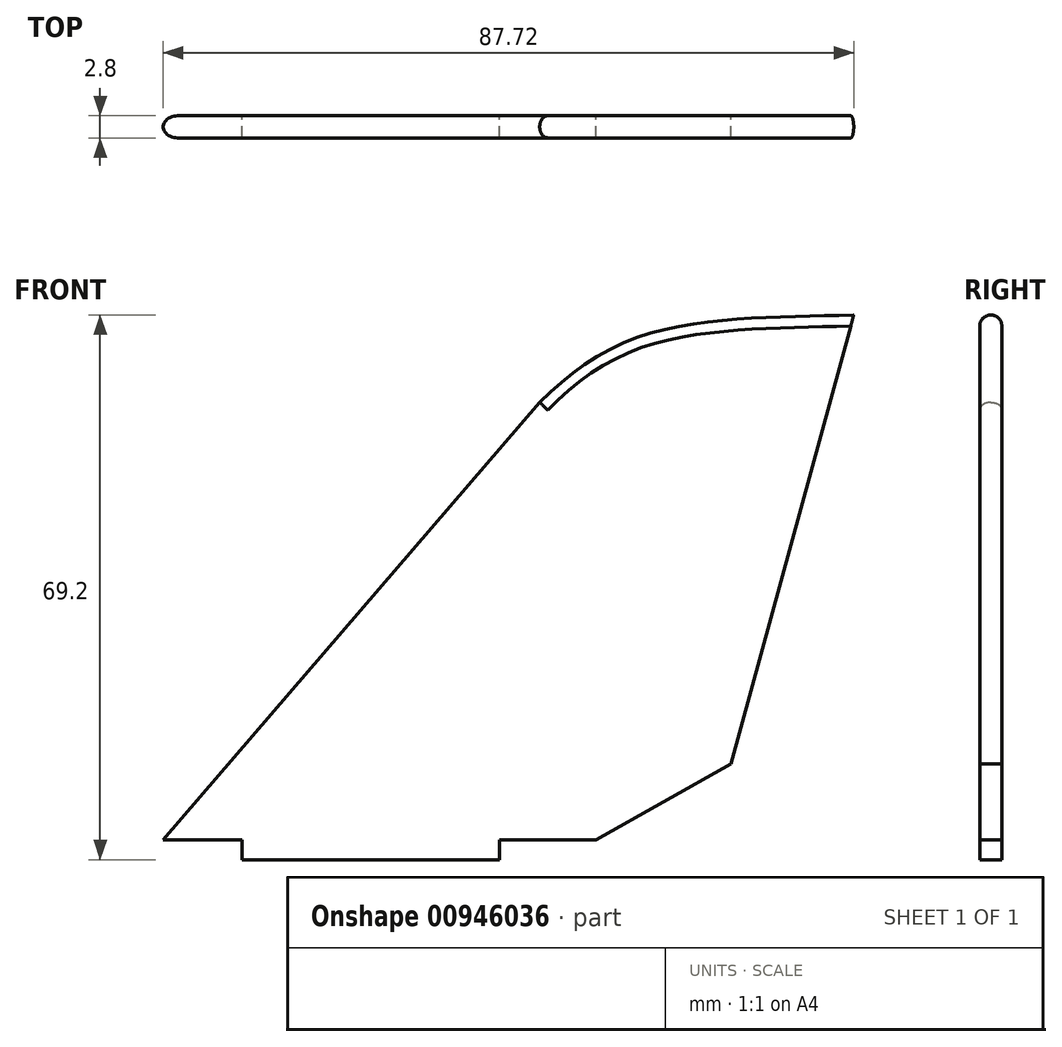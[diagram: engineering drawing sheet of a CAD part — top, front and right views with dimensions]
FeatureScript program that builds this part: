
annotation { "Feature Type Name" : "Feature", "Feature Type Description" : "" }
export const myFeature = defineFeature(function(context is Context, id is Id, definition is map)
    precondition{}
    {
        {
            var Q0;
            Q0=qCreatedBy(makeId("Front.planeOp"),FACE);
            var sketch = newSketch(context, id + "F0", { "sketchPlane" : qUnion([Q0])});
            skLineSegment(sketch, "E0.bottom", {"start": v(20, -28.75) * mm, "end": v(-35, -28.75) * mm});
            skLineSegment(sketch, "E0.right", {"start": v(-35, -28.75) * mm, "end": v(-35, -26.25) * mm});
            skPoint(sketch, "E0.middle", {"position": v(0, 0) * mm});
            skLineSegment(sketch, "E1", {"start": v(-35, -26.25) * mm, "end": v(-25, -26.25) * mm});
            skLineSegment(sketch, "E2", {"start": v(-35, -26.25) * mm, "end": v(3.21, 18.18) * mm});
            skPoint(sketch, "E3", {"position": v(20, -26.25) * mm});
            skPoint(sketch, "E4.orphan", {"position": v(-35, 28.75) * mm});
            skLineSegment(sketch, "E5", {"start": v(20, -26.25) * mm, "end": v(20, -28.75) * mm});
            skPoint(sketch, "E0.left.end.orphan", {"position": v(35, -8.81) * mm});
            skPoint(sketch, "E6.orphan", {"position": v(35, -28.75) * mm});
            skLineSegment(sketch, "E7", {"start": v(-25, -26.25) * mm, "end": v(-25, -28.75) * mm});
            skLineSegment(sketch, "E8", {"start": v(7.7, -26.25) * mm, "end": v(7.7, -28.75) * mm});
            skLineSegment(sketch, "E9.trimOffspring", {"start": v(7.7, -26.25) * mm, "end": v(20, -26.25) * mm});
            skLineSegment(sketch, "E10", {"start": v(20, -26.25) * mm, "end": v(37.1, -16.57) * mm});
            skLineSegment(sketch, "E11", {"start": v(37.1, -16.57) * mm, "end": v(52.72, 40.45) * mm});
            skLineSegment(sketch, "E12", {"start": v(-5.1, 8.52) * mm, "end": v(12.82, 29.35) * mm});
            skFitSpline(sketch, "E13", {"points": [v(12.82, 29.35) * mm, v(27.14, 38.2) * mm, v(52.72, 40.45) * mm], "startDerivative": vector(28.22, 28.29) * mm, "endDerivative": vector(48.68, 1.16) * mm});
            skSolve(sketch);
        }
        {
            var Q0;
            {var subQ1=sQuery(id+"F0.wireOp",EDGE,"E1");Q0=makeQuery(id+"F0.imprint","IMPRINT",FACE,{"disambiguationData":[TD([[makeQuery(id+"F0.imprint","IMPRINT",EDGE,{"derivedFrom":subQ1}),1.0]])]});}
            extrude(context, id + "F1", {"entities" : qUnion([Q0]), "depth" : 2.8 * mm, "offsetDistance" : 25 * mm});
        }
        {
            var Q0;
            Q0=makeQuery(id+"F1.opExtrude","CAP_EDGE",EDGE,{"disambiguationData":[OSD([sQuery(id+"F0.wireOp",EDGE,"E2")])],"isStart":false});
            var Q1;
            Q1=makeQuery(id+"F1.opExtrude","CAP_EDGE",EDGE,{"disambiguationData":[OSD([sQuery(id+"F0.wireOp",EDGE,"E2")])],"isStart":true});
            var Q2;
            Q2=makeQuery(id+"F1.opExtrude","CAP_EDGE",EDGE,{"disambiguationData":[OSD([sQuery(id+"F0.wireOp",EDGE,"effb0935-db41-4f9f-954a-b27e5b631a09")])],"isStart":false});
            var Q3;
            Q3=makeQuery(id+"F1.opExtrude","CAP_EDGE",EDGE,{"disambiguationData":[OSD([sQuery(id+"F0.wireOp",EDGE,"effb0935-db41-4f9f-954a-b27e5b631a09")])],"isStart":true});
            var Q4;
            Q4=makeQuery(id+"F1.opExtrude","CAP_EDGE",EDGE,{"disambiguationData":[OSD([sQuery(id+"F0.wireOp",EDGE,"E13")])],"isStart":false});
            var Q5;
            Q5=makeQuery(id+"F1.opExtrude","CAP_EDGE",EDGE,{"disambiguationData":[OSD([sQuery(id+"F0.wireOp",EDGE,"E13")])],"isStart":true});
            fillet(context, id + "F2", {"entities" : qUnion([Q0, Q1, Q2, Q3, Q4, Q5]), "radius" : 1.4 * mm, "tangentPropagation" : true, "allowEdgeOverflow" : false});
        }
    });
